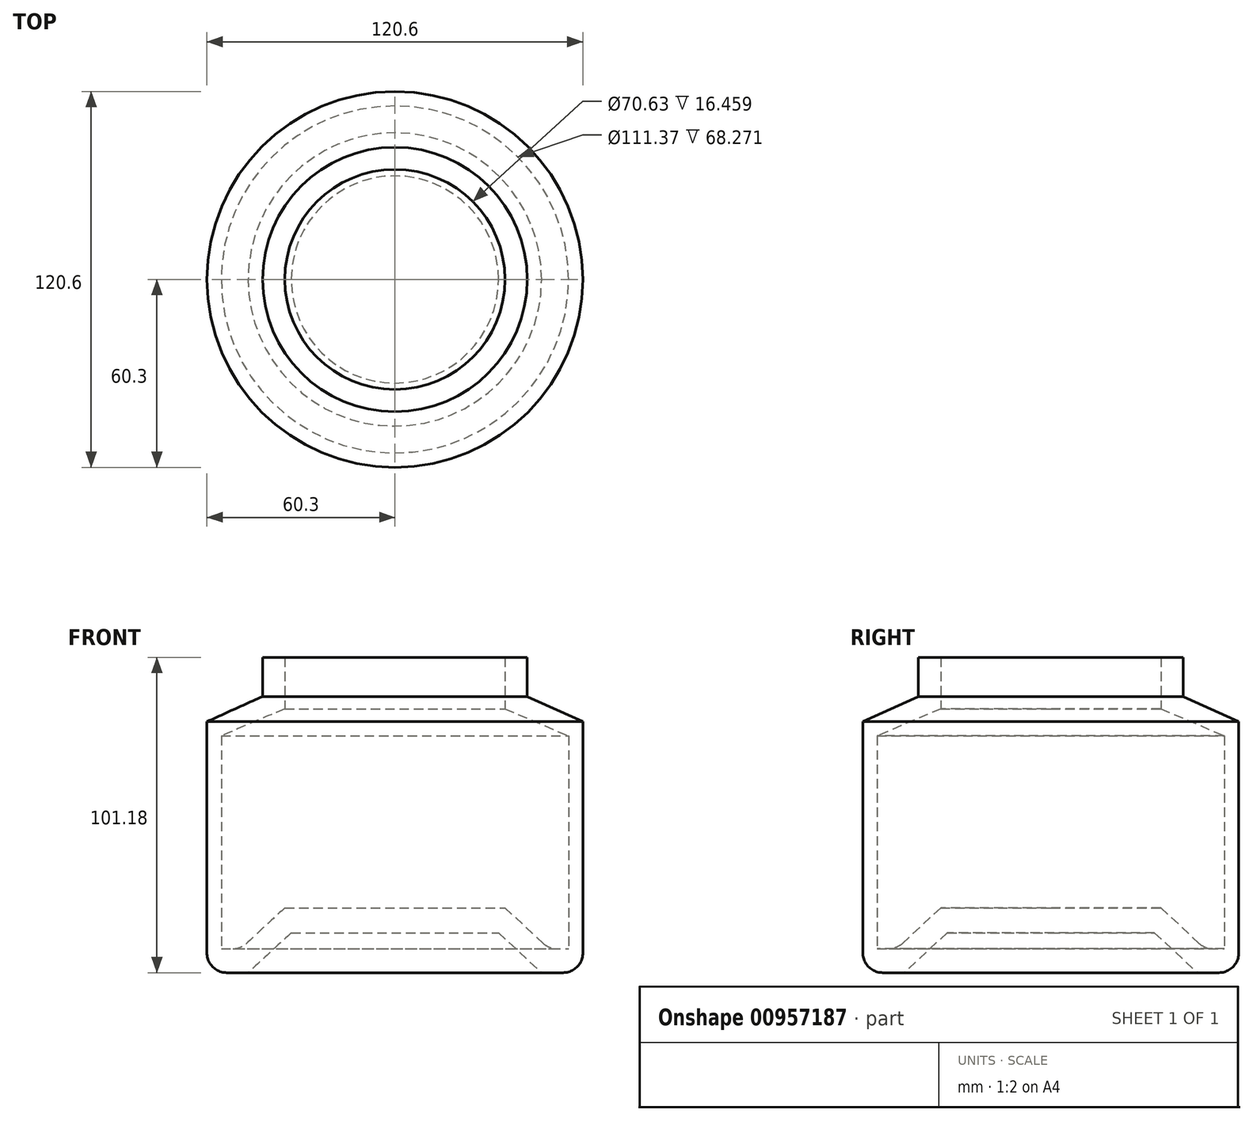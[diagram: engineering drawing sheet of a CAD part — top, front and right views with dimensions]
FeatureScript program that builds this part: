
annotation { "Feature Type Name" : "Feature", "Feature Type Description" : "" }
export const myFeature = defineFeature(function(context is Context, id is Id, definition is map)
    precondition{}
    {
        {
            var Q0;
            Q0=qCreatedBy(makeId("Front.planeOp"),FACE);
            var sketch = newSketch(context, id + "F0", { "sketchPlane" : qUnion([Q0])});
            skLineSegment(sketch, "E0", {"start": v(0, 0) * mm, "end": v(0, 66.63) * mm, "construction": true});
            skLineSegment(sketch, "E1", {"start": v(0, 0) * mm, "end": v(33.24, 0) * mm});
            skLineSegment(sketch, "E2", {"start": v(33.24, 0) * mm, "end": v(47.06, -12.8) * mm});
            skLineSegment(sketch, "E3", {"start": v(47.06, -12.8) * mm, "end": v(53.95, -12.8) * mm});
            skLineSegment(sketch, "E4", {"start": v(60.3, -6.46) * mm, "end": v(60.3, 67.78) * mm});
            skLineSegment(sketch, "E5", {"start": v(60.3, 67.78) * mm, "end": v(42.45, 75.84) * mm});
            skLineSegment(sketch, "E6", {"start": v(42.45, 75.84) * mm, "end": v(42.45, 88.37) * mm});
            skLineSegment(sketch, "E7", {"start": v(42.45, 88.37) * mm, "end": v(35.31, 88.37) * mm});
            skLineSegment(sketch, "E8", {"start": v(35.31, 88.37) * mm, "end": v(35.31, 71.9) * mm});
            skLineSegment(sketch, "E9", {"start": v(35.31, 71.9) * mm, "end": v(55.68, 63.18) * mm});
            skLineSegment(sketch, "E10", {"start": v(55.68, 63.18) * mm, "end": v(55.68, -5.1) * mm});
            skLineSegment(sketch, "E11", {"start": v(55.68, -5.1) * mm, "end": v(51.9, -5.1) * mm});
            skLineSegment(sketch, "E12", {"start": v(47.59, -3.4) * mm, "end": v(35.31, 8) * mm});
            skLineSegment(sketch, "E13", {"start": v(35.31, 8) * mm, "end": v(0, 8) * mm});
            skLineSegment(sketch, "E14", {"start": v(0, 8) * mm, "end": v(0, 0) * mm});
            skPoint(sketch, "E15.visualSharp", {"position": v(60.3, -12.8) * mm});
            skArc(sketch, "E15.filletArc", {"start": v(53.95, -12.8) * mm, "mid": v(58.44, -10.95) * mm, "end": v(60.3, -6.46) * mm});
            skPoint(sketch, "E16.visualSharp", {"position": v(49.42, -5.1) * mm});
            skArc(sketch, "E16.filletArc", {"start": v(47.59, -3.4) * mm, "mid": v(49.59, -4.66) * mm, "end": v(51.9, -5.1) * mm});
            skSolve(sketch);
        }
        {
            var Q0;
            Q0 = qSketchRegion(id + "F0", true);
            var Q1;
            Q1=sQuery(id+"F0.wireOp",EDGE,"E0");
            revolve(context, id + "F1", {"surfaceOperationType" : NewSurfaceOperationType.NEW, "entities" : qUnion([Q0]), "axis" : qUnion([Q1]), "revolveType" : RevolveType.FULL});
        }
    });
